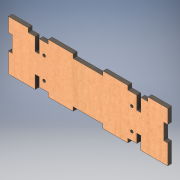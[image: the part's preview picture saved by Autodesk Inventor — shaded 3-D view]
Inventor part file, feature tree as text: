
AUTODESK INVENTOR PART (.ipt)
format: ipt  version: 2019 (Build 230136000, 136)  size: 190,464 bytes
history: native  units: mm
features: sketch x2, other x1, extrude x1, hole x1
ambient origin geometry x8: Origin, YZ Plane, XZ Plane, XY Plane, X Axis, Y Axis, Z Axis, Center Point
bodies: Body1 (feature_tree)
feature tree (5):
  other  "Твердое тело1"
  extrude  "Выдавливание1"  Depth=4.0mm
  hole  "Отверстие1"  [1 undecoded]
  sketch  "Эскиз1"
  sketch  "Эскиз3"
note: 1 required parameter value undecoded (feature->parameter linkage not recoverable at this tier; creation-order binding heuristic only, values carry confidence <= 0.55)
